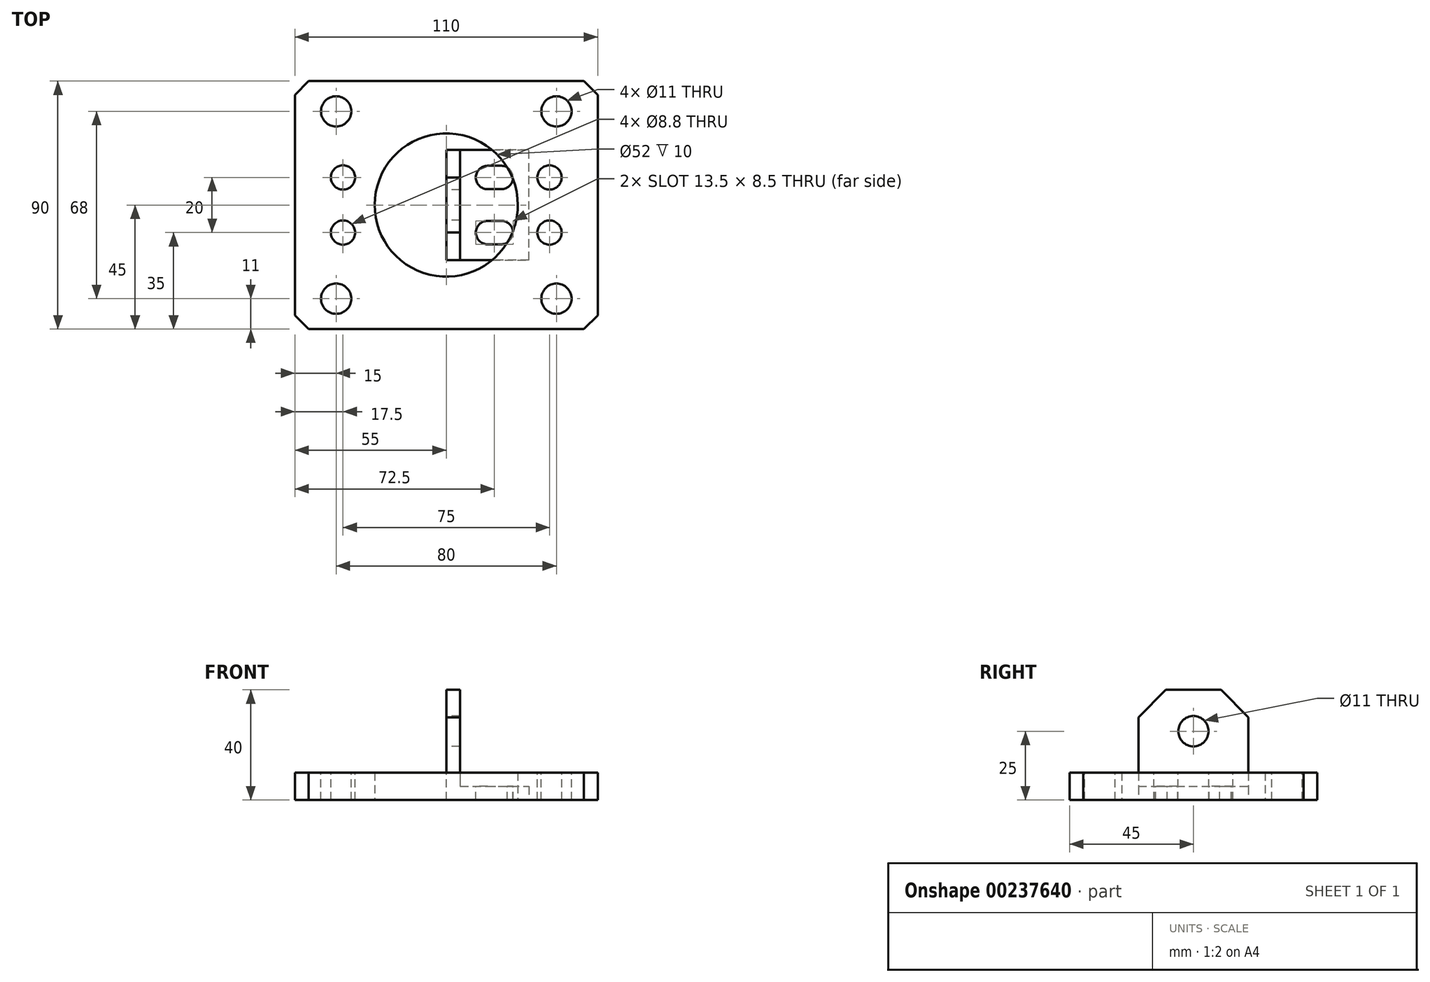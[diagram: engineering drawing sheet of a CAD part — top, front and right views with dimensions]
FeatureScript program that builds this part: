
annotation { "Feature Type Name" : "Feature", "Feature Type Description" : "" }
export const myFeature = defineFeature(function(context is Context, id is Id, definition is map)
    precondition{}
    {
        {
            var Q0;
            Q0=qCreatedBy(makeId("Top.planeOp"),FACE);
            var sketch = newSketch(context, id + "F0", { "sketchPlane" : qUnion([Q0])});
            skLineSegment(sketch, "E0.bottom", {"start": v(-55, 45) * mm, "end": v(55, 45) * mm});
            skLineSegment(sketch, "E0.top", {"start": v(-55, -45) * mm, "end": v(55, -45) * mm});
            skLineSegment(sketch, "E0.left", {"start": v(-55, 45) * mm, "end": v(-55, -45) * mm});
            skLineSegment(sketch, "E0.right", {"start": v(55, 45) * mm, "end": v(55, -45) * mm});
            skPoint(sketch, "E1", {"position": v(0, 0) * mm});
            skCircle(sketch, "E2", {"center": v(0, 0) * mm, "radius": 26 * mm});
            skSolve(sketch);
        }
        {
            var Q0;
            Q0 = qSketchRegion(id + "F0", true);
            extrude(context, id + "F1", {"entities" : qUnion([Q0]), "depth" : 10 * mm});
        }
        {
            var Q0;
            Q0=makeQuery(id+"F1.opExtrude","CAP_FACE",FACE,{"disambiguationData":[OSD([sQuery(id+"F0.wireOp",EDGE,"E0.bottom"),sQuery(id+"F0.wireOp",EDGE,"E0.top"),sQuery(id+"F0.wireOp",EDGE,"E0.left"),sQuery(id+"F0.wireOp",EDGE,"E0.right")])],"isStart":false});
            var sketch = newSketch(context, id + "F2", { "sketchPlane" : qUnion([Q0])});
            skPoint(sketch, "E3", {"position": v(-40, 34) * mm});
            skPoint(sketch, "E4", {"position": v(40, 34) * mm});
            skPoint(sketch, "E5", {"position": v(40, -34) * mm});
            skPoint(sketch, "E6", {"position": v(-40, -34) * mm});
            skPoint(sketch, "E7", {"position": v(0, 0) * mm});
            skSolve(sketch);
        }
        {
            var Q0;
            Q0=sQuery(id+"F2.wireOp",VERTEX,"E3");
            var Q1;
            Q1=sQuery(id+"F2.wireOp",VERTEX,"E6");
            var Q2;
            Q2=sQuery(id+"F2.wireOp",VERTEX,"E5");
            var Q3;
            Q3=sQuery(id+"F2.wireOp",VERTEX,"E4");
            var Q4;
            Q4=makeQuery(id+"F1.opExtrude","SWEPT_BODY",BODY,{"disambiguationData":[OSD([sQuery(id+"F0.wireOp",EDGE,"E0.bottom"),sQuery(id+"F0.wireOp",EDGE,"E0.top"),sQuery(id+"F0.wireOp",EDGE,"E0.left"),sQuery(id+"F0.wireOp",EDGE,"E0.right")])]});
            hole(context, id + "F3", {"style" : HoleStyle.SIMPLE, "endStyle" : HoleEndStyle.THROUGH, "standardTappedOrClearance" : lookupTablePath({ "standard" : "ISO", "fit" : "Normal", "size" : "M10", "type" : "Clearance" }), "standardBlindInLast" : lookupTablePath({ "fit" : "Standard", "standard" : "ISO", "size" : "M10", "type" : "Clearance" }), "holeDiameter" : 11 * mm, "locations" : qUnion([Q0, Q1, Q2, Q3]), "scope" : qUnion([Q4]), "isTappedThrough" : true});
        }
        {
            var Q0;
            Q0=qCreatedBy(makeId("Front.planeOp"),FACE);
            var sketch = newSketch(context, id + "F4", { "sketchPlane" : qUnion([Q0])});
            skLineSegment(sketch, "E8", {"start": v(0, 0) * mm, "end": v(0, 40) * mm});
            skLineSegment(sketch, "E9", {"start": v(0, 40) * mm, "end": v(5, 40) * mm});
            skLineSegment(sketch, "E10", {"start": v(5, 40) * mm, "end": v(5, 5) * mm});
            skLineSegment(sketch, "E11", {"start": v(5, 5) * mm, "end": v(30, 5) * mm});
            skLineSegment(sketch, "E12", {"start": v(30, 5) * mm, "end": v(30, 0) * mm});
            skLineSegment(sketch, "E13", {"start": v(30, 0) * mm, "end": v(0, 0) * mm});
            skSolve(sketch);
        }
        {
            var Q0;
            Q0 = qSketchRegion(id + "F4", true);
            extrude(context, id + "F5", {"entities" : qUnion([Q0]), "endBound" : BoundingType.SYMMETRIC, "depth" : 40 * mm});
        }
        {
            var Q0;
            Q0=makeQuery(id+"F5.opExtrude","SWEPT_FACE",FACE,{"disambiguationData":[OSD([sQuery(id+"F4.wireOp",EDGE,"E8")])]});
            var sketch = newSketch(context, id + "F6", { "sketchPlane" : qUnion([Q0])});
            skPoint(sketch, "E14", {"position": v(0, 25) * mm});
            skSolve(sketch);
        }
        {
            var Q0;
            Q0=sQuery(id+"F6.wireOp",VERTEX,"E14");
            var Q1;
            Q1=makeQuery(id+"F5.opExtrude","SWEPT_BODY",BODY,{"disambiguationData":[OSD([sQuery(id+"F4.wireOp",EDGE,"E8"),sQuery(id+"F4.wireOp",EDGE,"E9"),sQuery(id+"F4.wireOp",EDGE,"E10"),sQuery(id+"F4.wireOp",EDGE,"E11"),sQuery(id+"F4.wireOp",EDGE,"E12"),sQuery(id+"F4.wireOp",EDGE,"E13")])]});
            hole(context, id + "F7", {"style" : HoleStyle.SIMPLE, "endStyle" : HoleEndStyle.THROUGH, "holeDiameter" : 11 * mm, "locations" : qUnion([Q0]), "scope" : qUnion([Q1]), "isTappedThrough" : true});
        }
        {
            var Q0;
            Q0=makeQuery(id+"F5.opExtrude","CAP_EDGE",EDGE,{"disambiguationData":[OSD([sQuery(id+"F4.wireOp",EDGE,"E9")])],"isStart":false});
            var Q1;
            Q1=makeQuery(id+"F5.opExtrude","CAP_EDGE",EDGE,{"disambiguationData":[OSD([sQuery(id+"F4.wireOp",EDGE,"E9")])],"isStart":true});
            chamfer(context, id + "F8", {"entities" : qUnion([Q0, Q1]), "width" : 10 * mm, "tangentPropagation" : true});
        }
        {
            var Q0;
            Q0=makeQuery(id+"F5.opExtrude","SWEPT_FACE",FACE,{"disambiguationData":[OSD([sQuery(id+"F4.wireOp",EDGE,"E11")])]});
            var sketch = newSketch(context, id + "F9", { "sketchPlane" : qUnion([Q0])});
            skArc(sketch, "E15", {"start": v(20, 5.75) * mm, "mid": v(24.25, 10) * mm, "end": v(20, 14.25) * mm});
            skArc(sketch, "E16", {"start": v(15, 14.25) * mm, "mid": v(10.75, 10) * mm, "end": v(15, 5.75) * mm});
            skArc(sketch, "E17", {"start": v(15, -5.75) * mm, "mid": v(10.75, -10) * mm, "end": v(15, -14.25) * mm});
            skArc(sketch, "E18", {"start": v(20, -14.25) * mm, "mid": v(24.25, -10) * mm, "end": v(20, -5.75) * mm});
            skLineSegment(sketch, "E19", {"start": v(15, 14.25) * mm, "end": v(20, 14.25) * mm});
            skLineSegment(sketch, "E20", {"start": v(20, 5.75) * mm, "end": v(15, 5.75) * mm});
            skLineSegment(sketch, "E21", {"start": v(15, -5.75) * mm, "end": v(20, -5.75) * mm});
            skLineSegment(sketch, "E22", {"start": v(20, -14.25) * mm, "end": v(15, -14.25) * mm});
            skSolve(sketch);
        }
        {
            var Q0;
            Q0 = qSketchRegion(id + "F9", true);
            extrude(context, id + "F10", {"entities" : qUnion([Q0]), "operationType" : NewBodyOperationType.REMOVE, "oppositeDirection" : true, "depth" : 25 * mm});
        }
        {
            var Q0;
            Q0=makeQuery(id+"F1.opExtrude","CAP_FACE",FACE,{"disambiguationData":[OSD([sQuery(id+"F0.wireOp",EDGE,"E0.bottom"),sQuery(id+"F0.wireOp",EDGE,"E0.top"),sQuery(id+"F0.wireOp",EDGE,"E0.left"),sQuery(id+"F0.wireOp",EDGE,"E0.right")])],"isStart":false});
            var sketch = newSketch(context, id + "F11", { "sketchPlane" : qUnion([Q0])});
            skPoint(sketch, "E23", {"position": v(-37.5, 10) * mm});
            skPoint(sketch, "E24", {"position": v(-37.5, -10) * mm});
            skPoint(sketch, "E25", {"position": v(37.5, -10) * mm});
            skPoint(sketch, "E26", {"position": v(37.5, 10) * mm});
            skSolve(sketch);
        }
        {
            var Q0;
            Q0=sQuery(id+"F11.wireOp",VERTEX,"E23");
            var Q1;
            Q1=sQuery(id+"F11.wireOp",VERTEX,"E24");
            var Q2;
            Q2=sQuery(id+"F11.wireOp",VERTEX,"E25");
            var Q3;
            Q3=sQuery(id+"F11.wireOp",VERTEX,"E26");
            var Q4;
            Q4=makeQuery(id+"F1.opExtrude","SWEPT_BODY",BODY,{"disambiguationData":[OSD([sQuery(id+"F0.wireOp",EDGE,"E0.bottom"),sQuery(id+"F0.wireOp",EDGE,"E0.top"),sQuery(id+"F0.wireOp",EDGE,"E0.left"),sQuery(id+"F0.wireOp",EDGE,"E0.right")])]});
            hole(context, id + "F12", {"style" : HoleStyle.SIMPLE, "endStyle" : HoleEndStyle.THROUGH, "standardTappedOrClearance" : lookupTablePath({ "standard" : "ISO", "fit" : "Normal", "size" : "M8", "type" : "Clearance" }), "standardBlindInLast" : lookupTablePath({ "fit" : "Standard", "standard" : "ISO", "size" : "M8", "type" : "Clearance" }), "holeDiameter" : 8.8 * mm, "locations" : qUnion([Q0, Q1, Q2, Q3]), "scope" : qUnion([Q4]), "isTappedThrough" : true});
        }
        {
            var Q0;
            Q0=makeQuery(id+"F1.opExtrude","SWEPT_EDGE",EDGE,{"disambiguationData":[OSD([sQuery(id+"F0.wireOp",EDGE,"E0.bottom"),sQuery(id+"F0.wireOp",EDGE,"E0.left")])]});
            var Q1;
            Q1=makeQuery(id+"F1.opExtrude","SWEPT_EDGE",EDGE,{"disambiguationData":[OSD([sQuery(id+"F0.wireOp",EDGE,"E0.bottom"),sQuery(id+"F0.wireOp",EDGE,"E0.right")])]});
            var Q2;
            Q2=makeQuery(id+"F1.opExtrude","SWEPT_EDGE",EDGE,{"disambiguationData":[OSD([sQuery(id+"F0.wireOp",EDGE,"E0.top"),sQuery(id+"F0.wireOp",EDGE,"E0.right")])]});
            var Q3;
            Q3=makeQuery(id+"F1.opExtrude","SWEPT_EDGE",EDGE,{"disambiguationData":[OSD([sQuery(id+"F0.wireOp",EDGE,"E0.top"),sQuery(id+"F0.wireOp",EDGE,"E0.left")])]});
            chamfer(context, id + "F13", {"entities" : qUnion([Q0, Q1, Q2, Q3]), "width" : 5 * mm, "tangentPropagation" : true});
        }
    });
